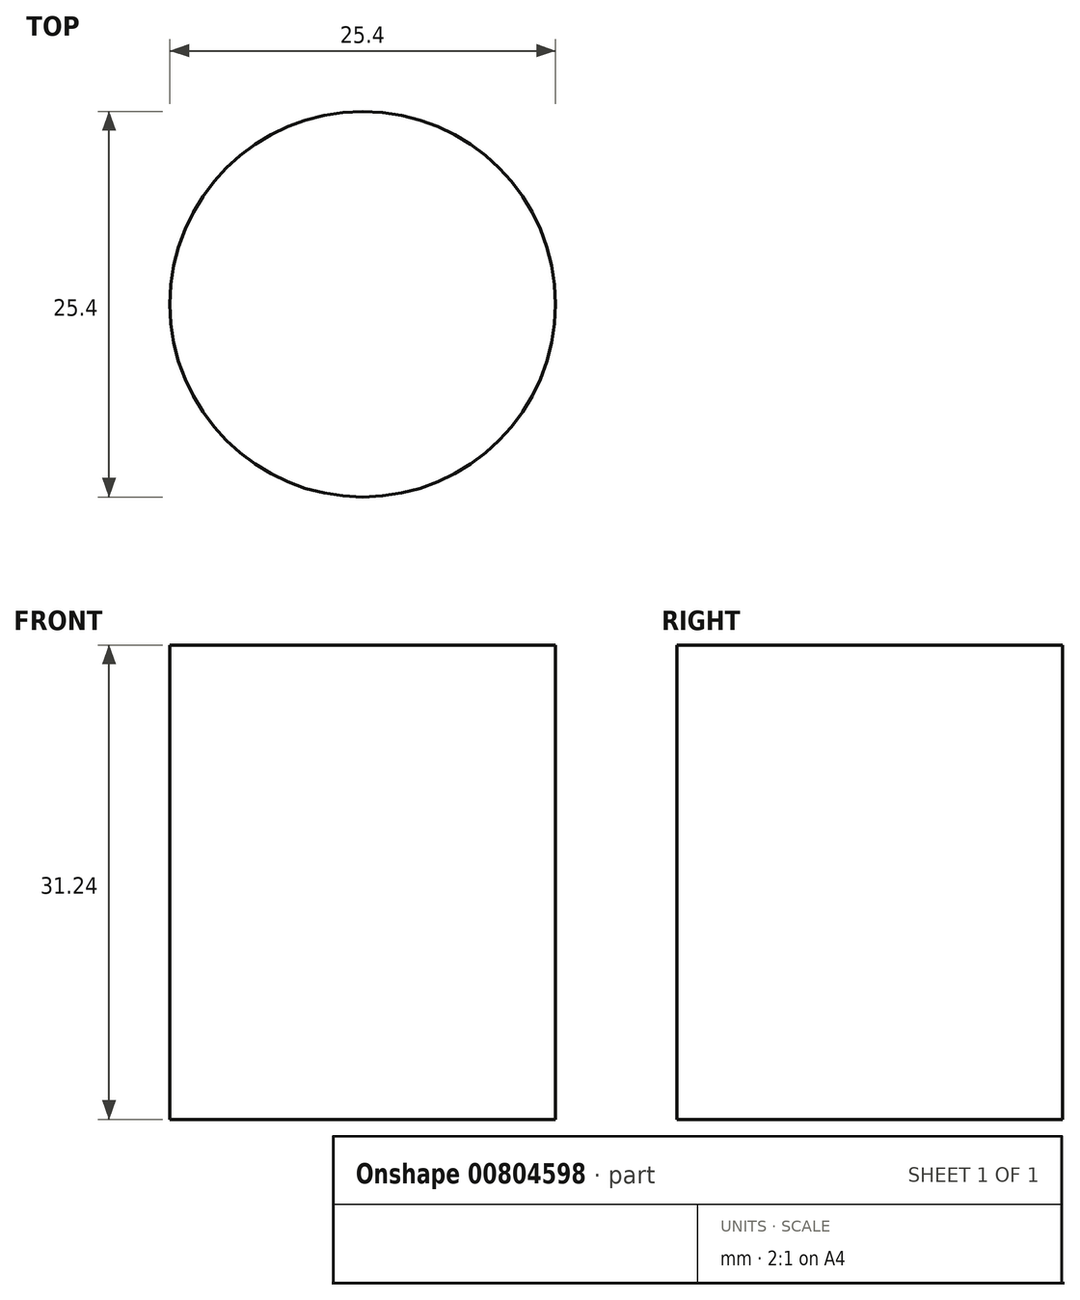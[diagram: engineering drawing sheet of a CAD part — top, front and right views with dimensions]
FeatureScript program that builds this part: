
annotation { "Feature Type Name" : "Feature", "Feature Type Description" : "" }
export const myFeature = defineFeature(function(context is Context, id is Id, definition is map)
    precondition{}
    {
        {
            var Q0;
            Q0=qCreatedBy(makeId("Top.planeOp"),FACE);
            var sketch = newSketch(context, id + "F0", { "sketchPlane" : qUnion([Q0])});
            skCircle(sketch, "E0", {"center": v(0, 0) * mm, "radius": 12.7 * mm});
            skSolve(sketch);
        }
        {
            var Q0;
            Q0 = qSketchRegion(id + "F0", true);
            extrude(context, id + "F1", {"entities" : qUnion([Q0]), "depth" : 31.24 * mm, "offsetDistance" : 25.4 * mm});
        }
    });
